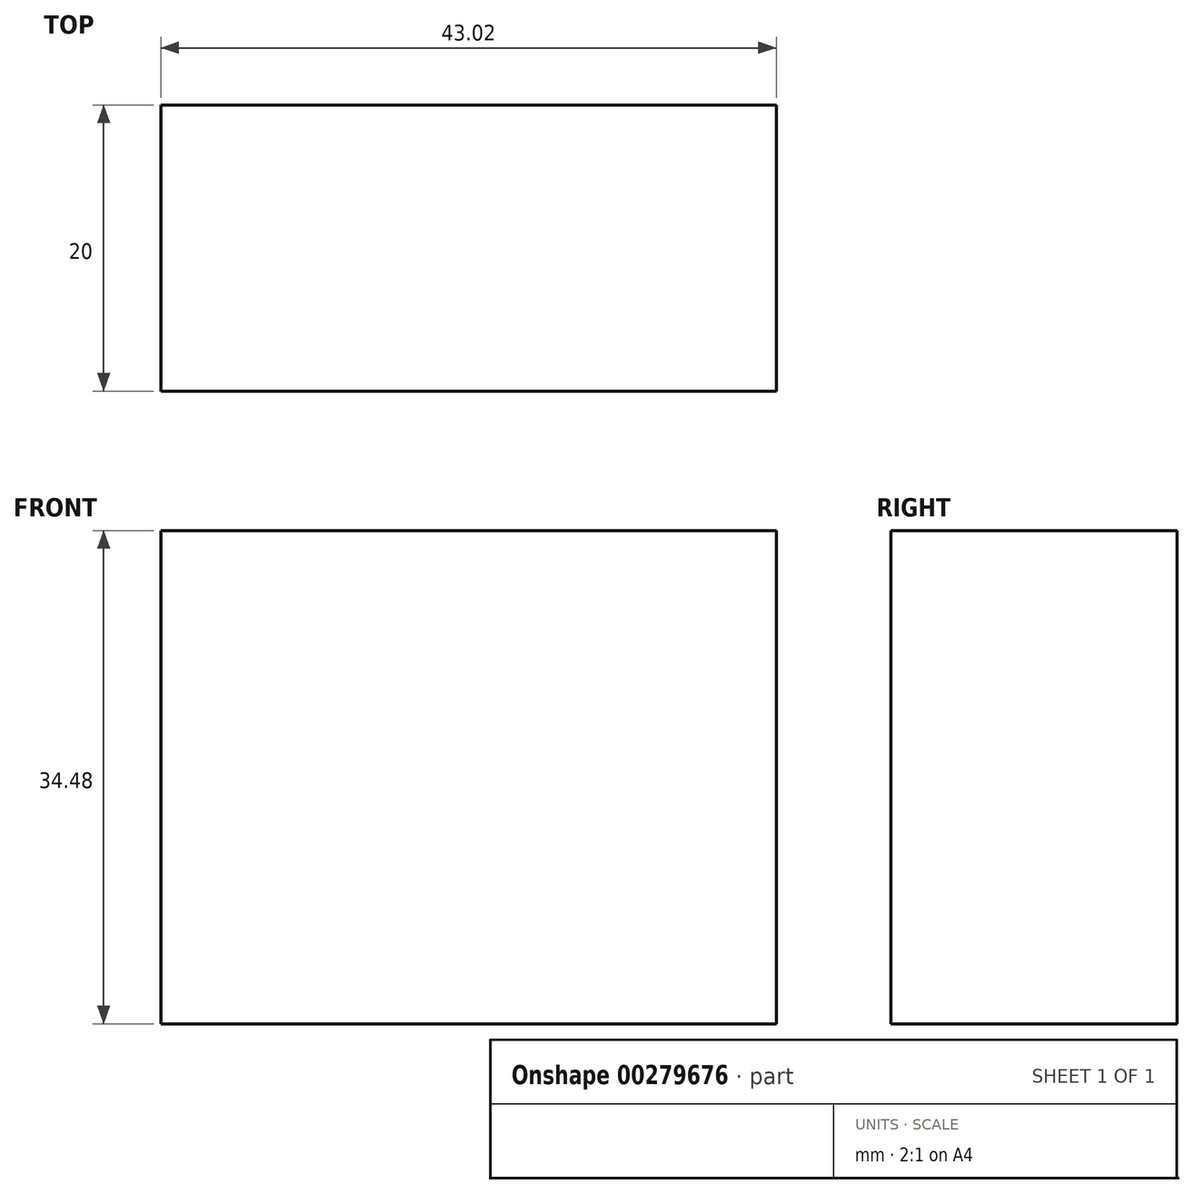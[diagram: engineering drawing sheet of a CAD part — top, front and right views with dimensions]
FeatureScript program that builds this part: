
annotation { "Feature Type Name" : "Feature", "Feature Type Description" : "" }
export const myFeature = defineFeature(function(context is Context, id is Id, definition is map)
    precondition{}
    {
        {
            var Q0;
            Q0=qCreatedBy(makeId("Front.planeOp"),FACE);
            var sketch = newSketch(context, id + "F0", { "sketchPlane" : qUnion([Q0])});
            skLineSegment(sketch, "E0.bottom", {"start": v(0, 0) * mm, "end": v(43.02, 0) * mm});
            skLineSegment(sketch, "E0.top", {"start": v(0, 34.48) * mm, "end": v(43.02, 34.48) * mm});
            skLineSegment(sketch, "E0.left", {"start": v(0, 0) * mm, "end": v(0, 34.48) * mm});
            skLineSegment(sketch, "E0.right", {"start": v(43.02, 0) * mm, "end": v(43.02, 34.48) * mm});
            skSolve(sketch);
        }
        {
            var Q0;
            Q0=makeQuery(id+"F0.imprint","IMPRINT",FACE,{"disambiguationData":[TD([[makeQuery(id+"F0.imprint","IMPRINT",EDGE,{"derivedFrom":sQuery(id+"F0.wireOp",EDGE,"E0.bottom")}),1.0]])]});
            extrude(context, id + "F1", {"entities" : qUnion([Q0]), "depth" : 20 * mm});
        }
    });
